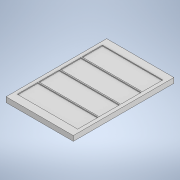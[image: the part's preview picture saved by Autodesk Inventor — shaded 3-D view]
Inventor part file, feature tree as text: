
AUTODESK INVENTOR PART (.ipt)
format: ipt  version: 2020 (Build 240168000, 168)  size: 130,560 bytes
history: native  units: in
note: dims shown in document units (in); Inventor stores cm internally (conversion verified against a paired STEP export)
features: extrude x2, sketch x2, pattern_linear x1
ambient origin geometry x8: Origin, YZ Plane, XZ Plane, XY Plane, X Axis, Y Axis, Z Axis, Center Point
bodies: Solid1 (feature_tree)
feature tree (5):
  extrude  "Extrusion1"  Depth=5.0299in
  extrude  "Extrusion2"  Depth=1.0787in
  pattern_linear  "Rectangular Pattern2"  Spacing1=0.25in  [1 undecoded]
  sketch  "Sketch1"  dims[d0=3.3654in d1=5.0299in]
  sketch  "Sketch3"  dims[d3=45.0deg d4=0.375in d5=0.25in d6=0.0in d23=0.1725in d24=0.387in d25=3.02in d26=1.0197in d27=0.0394in d28=0.0394in d29=0.0394in d30=0.0in d31=0.3937in d33=1.0787in d34=1.5748in d36=1.0787in]
note: 1 required parameter value undecoded (feature->parameter linkage not recoverable at this tier; creation-order binding heuristic only, values carry confidence <= 0.55)
